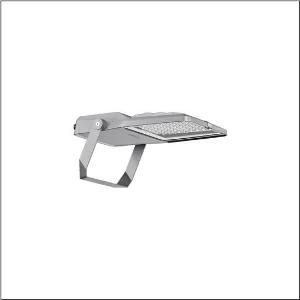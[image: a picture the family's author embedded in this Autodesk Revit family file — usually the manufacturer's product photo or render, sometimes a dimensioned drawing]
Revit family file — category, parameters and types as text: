
# Revit family: floodlight_fl_21_iq_mini___pl61_5xa7772d4c1a_f35a
name_source: partatom
category: Lighting Fixtures
units: mm (PartAtom-declared; Revit-internal decimal feet)

## family parameters
Cut with Voids When Loaded = No
Host = Face
Light Source = No
Part Type = Normal
Room Calculation Point = No
Round Connector Dimension = Use Diameter
Shared = No

## types (1)
- --- (1 x LED, 18260 lm, 143 W, 4000K)
    Apparent Load = 143 VA
    CIE Flux Codes = 33 65 98 100 100
    Color Rendering = 70
    Color Temperature = 4000K
    Default Elevation = 1800 mm
    Description = Floodlight FL 21 iQ mini, floodlight, primary light control with lens, of PMMA, primary optical cover: protective disc, of toughened safety glass, transparent, light distribution: PL61, light emission: direct distribution, installation type: surface-mounted, lamps: LED, High Power LED, rated values: 18.260lm | 143W | 127,7lm/W (begin service life); end service life: 18.260lm | 151,6W; at 50% lumin. flux: 9.130lm | 60,8W | 150,2lm/W, colour temperature: 4000K, colour rendering: CRI > 70, light colour: 740, light setting 1 begin service life: 100% | 18.260lm | 143W | 127,7lm/W | 4.000K, light setting 1 end service life: 151,6W, further light settings possible, control: Street-Remote, Auto-Match, Temp-Guard, Night-Set, Smart-Wire, Desk-Remote (wireless, voltage-free reading and setting of iQ features in the workshop via application-optimized NFC function/RFID function), optimised constant luminous flux control (CLO 2.0), pre-setting: linear dimming characteristic, with terminal, 6-pole, mains connection: 220..240V, AC, 50/60Hz, luminaire housing, of diecast aluminium, powder-coated, SITECO metallic grey (DB 702S), corrosivity category C5 mid according to DIN EN ISO 12944suitable for swimming poolschlorine-resistant, sealing non-destructively replaceable, mounting bracket, of steel, galvanised, powder-coated, SITECO metallic grey (DB 702S), protection rating (complete): IP66, insulation class (complete): insulation class II (safety insulation), certification: CE, ENEC, VDE, protection symbol: D, impact resistance: IK08, permissible operating ambient temperature: -40..+40°C, permissible operating ambient temperature for outdoor applications: -40..+50°C, standard: DIN EN 12944, LABS conformity tested according to VDMA 24364:2018-05, packaging unit: 1 piece

Light Distribution: PL61
    Height = 70 mm
    Lamp = 1 x LED
    Lamp Light Flux = 18260 lm
    Lamp Power = 143 W
    Lamp count = 1
    Length = 485 mm
    Luminous efficacy = 128 lm/W
    Manufacturer = Siteco
    ModVariant = No
    Model = 5XA7772D4C1A
    Mounting Place = Pole
    Mounting Type = Pole annexe
    Number of Poles = 1
    OnlyDefault = Yes
    Power Factor = 1
    Product Name = Floodlight FL 21 iQ mini | PL61
    Product group = floodlight | pylon annexe
    ProductGroupID = 6201
    Protection Class = Protection class II
    Protection Degree = IP 66
    RLX_Detail_Level = 1
    RLX_Emergency_Light_Flux = 0 lm
    RLX_Emergency_Type = 0
    RLX_Emergency_Type_DB = No
    RlxData = <blob elided: 96881 chars, md5=01c42d1e>
    Socket = socket
    Standby Power = 0 W
    System Light Flux = 18260 lm
    System Power = 143 W
    Type Comments = factory setting: luminous flux: 100 % | dim-lin: 254 | 730 mA
    Type Image = l_1006845.jpg
    URL = http://relux.com
    VarID = @adj_173417
    Voltage = 0 V
    Weight = 0.00 kg
    Width = 337 mm

## geometry (parser evidence)
native form markers: Blend x4, Sweep x13
no freeform markers — native parametric forms only
